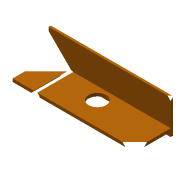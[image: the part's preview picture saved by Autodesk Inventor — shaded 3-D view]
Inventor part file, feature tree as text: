
AUTODESK INVENTOR PART (.ipt)
format: ipt  version: 2016 (Build 200138000, 138)  size: 117,248 bytes
history: native  units: in
note: dims shown in document units (in); Inventor stores cm internally (conversion verified against a paired STEP export)
features: sketch x7, other x3, plane x1
ambient origin geometry x8: Origin, YZ Plane, XZ Plane, XY Plane, X Axis, Y Axis, Z Axis, Center Point
bodies: Solid1 (feature_tree)
feature tree (11):
  other  "P_hips02_001.ipt"
  other  "Solid1::P_hips02_001.ipt"
  other  "TaggingFeature1"
  sketch  "Sketch1"  dims[d0=0.3937in]
  sketch  "Sketch3"
  sketch  "Sketch4"
  sketch  "Sketch5"
  sketch  "Sketch6"
  sketch  "Sketch8"
  sketch  "Sketch9"
  plane  "Work Plane1"
